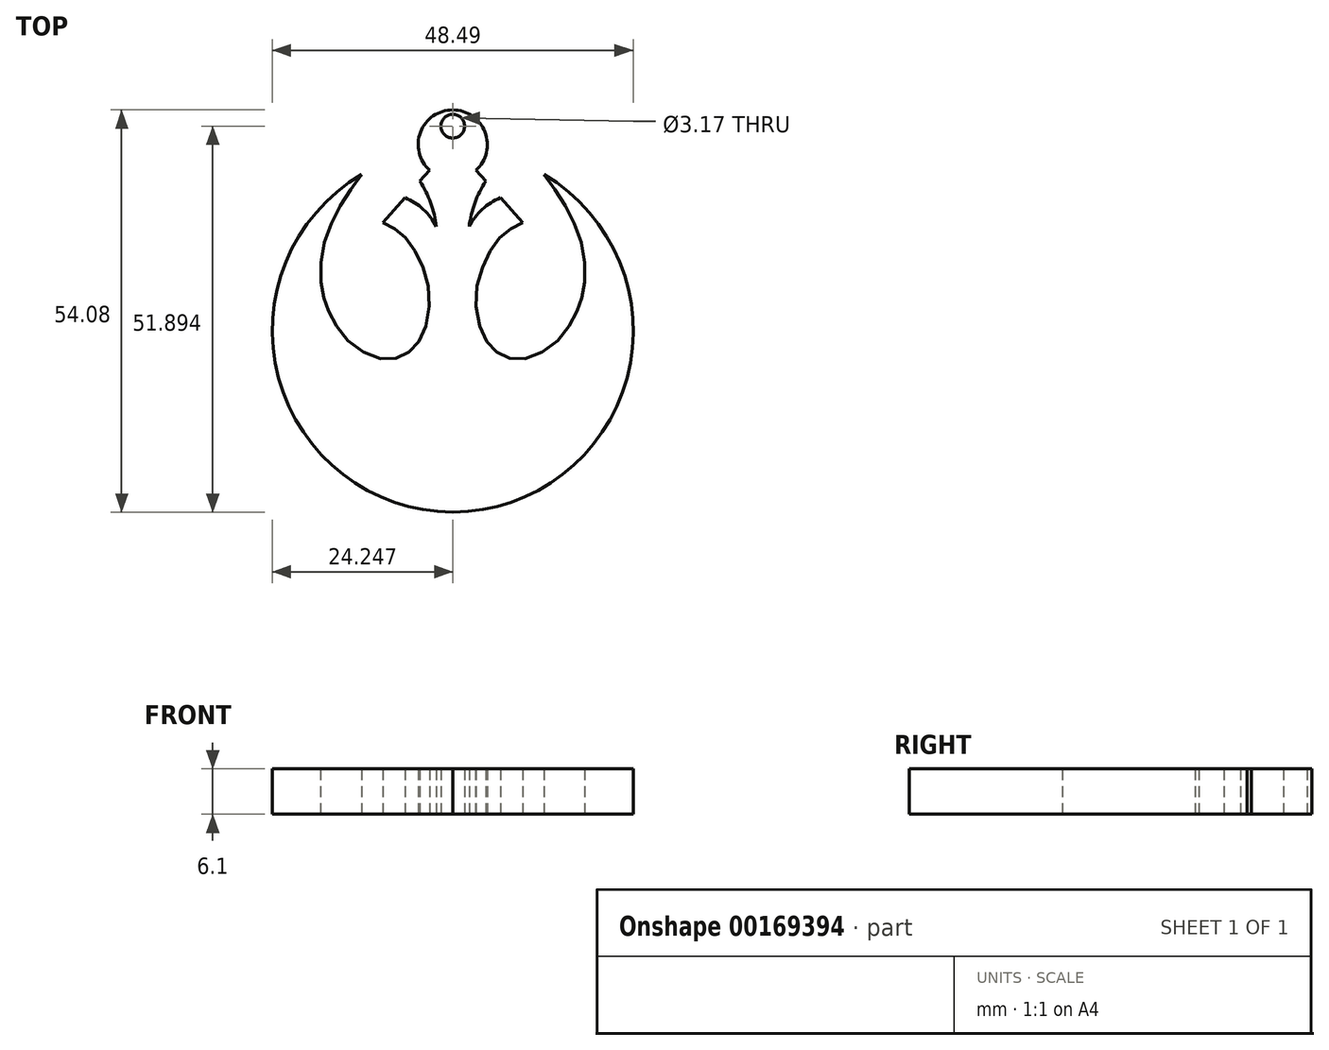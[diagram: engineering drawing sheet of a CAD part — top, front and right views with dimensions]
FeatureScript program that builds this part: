
annotation { "Feature Type Name" : "Feature", "Feature Type Description" : "" }
export const myFeature = defineFeature(function(context is Context, id is Id, definition is map)
    precondition{}
    {
        {
            var Q0;
            Q0=qCreatedBy(makeId("Top.planeOp"),FACE);
            var sketch = newSketch(context, id + "F0", { "sketchPlane" : qUnion([Q0])});
            skLineSegment(sketch, "E0", {"start": v(-5.57, 17) * mm, "end": v(-6.9, 15.52) * mm});
            skArc(sketch, "E1", {"start": v(-4.67, 9.44) * mm, "mid": v(-5.43, 12.61) * mm, "end": v(-6.9, 15.52) * mm});
            skArc(sketch, "E2", {"start": v(-4.67, 9.44) * mm, "mid": v(-6.43, 11.75) * mm, "end": v(-8.88, 13.3) * mm});
            skLineSegment(sketch, "E3", {"start": v(-8.88, 13.3) * mm, "end": v(-11.87, 9.97) * mm});
            skFitSpline(sketch, "E4", {"points": [v(-11.87, 9.97) * mm, v(-9.47, 8.58) * mm, v(-7.17, 5.54) * mm, v(-5.6, 0.31) * mm, v(-6.6, -5.27) * mm, v(-8.75, -7.7) * mm, v(-11.87, -8.35) * mm, v(-16.37, -6.1) * mm, v(-19.06, -2.12) * mm, v(-20.03, 0.88) * mm, v(-19.95, 6.25) * mm, v(-17.73, 11.98) * mm, v(-14.7, 16.46) * mm], "startDerivative": vector(37.66, -17.5) * mm, "endDerivative": vector(34.42, 46.42) * mm});
            skArc(sketch, "E5", {"start": v(-14.7, 16.46) * mm, "mid": v(-25.87, -10.91) * mm, "end": v(-2.46, -28.97) * mm});
            skArc(sketch, "E6.MirrorCS", {"start": v(9.77, 16.46) * mm, "mid": v(20.94, -10.91) * mm, "end": v(-2.46, -28.97) * mm});
            skFitSpline(sketch, "E7.MirrorCS", {"points": [v(6.94, 9.97) * mm, v(4.54, 8.58) * mm, v(2.25, 5.54) * mm, v(0.67, 0.31) * mm, v(1.68, -5.27) * mm, v(3.82, -7.7) * mm, v(6.94, -8.35) * mm, v(11.45, -6.1) * mm, v(14.13, -2.12) * mm, v(15.1, 0.88) * mm, v(15.03, 6.25) * mm, v(12.8, 11.98) * mm, v(9.77, 16.46) * mm], "startDerivative": vector(-37.66, -17.5) * mm, "endDerivative": vector(-34.42, 46.42) * mm});
            skLineSegment(sketch, "E8.MirrorCS", {"start": v(0.64, 17) * mm, "end": v(1.97, 15.52) * mm});
            skLineSegment(sketch, "E9.MirrorCS", {"start": v(3.96, 13.3) * mm, "end": v(6.94, 9.97) * mm});
            skArc(sketch, "E10.MirrorCS", {"start": v(-0.26, 9.44) * mm, "mid": v(1.5, 11.75) * mm, "end": v(3.96, 13.3) * mm});
            skArc(sketch, "E11.MirrorCS", {"start": v(-0.26, 9.44) * mm, "mid": v(0.5, 12.61) * mm, "end": v(1.97, 15.52) * mm});
            skArc(sketch, "E12", {"start": v(0.64, 17) * mm, "mid": v(-2.46, 25.11) * mm, "end": v(-5.57, 17) * mm});
            skCircle(sketch, "E13", {"center": v(-2.46, 22.92) * mm, "radius": 1.59 * mm});
            skSolve(sketch);
        }
        {
            var Q0;
            {var subQ5=sQuery(id+"F0.wireOp",EDGE,"E1");Q0=makeQuery(id+"F0.imprint","IMPRINT",FACE,{"disambiguationData":[TD([[makeQuery(id+"F0.imprint","IMPRINT",EDGE,{"derivedFrom":subQ5}),-1.0]])]});}
            extrude(context, id + "F1", {"entities" : qUnion([Q0]), "depth" : 6.1 * mm});
        }
        {
            var Q0;
            {var subQ3=sQuery(id+"F0.wireOp",EDGE,"E12");Q0=makeQuery(id+"F0.imprint","IMPRINT",FACE,{"disambiguationData":[TD([[makeQuery(id+"F0.imprint","IMPRINT",EDGE,{"derivedFrom":subQ3}),1.0]])]});}
            extrude(context, id + "F2", {"entities" : qUnion([Q0]), "operationType" : NewBodyOperationType.ADD, "depth" : 3.8 * mm});
        }
    });
